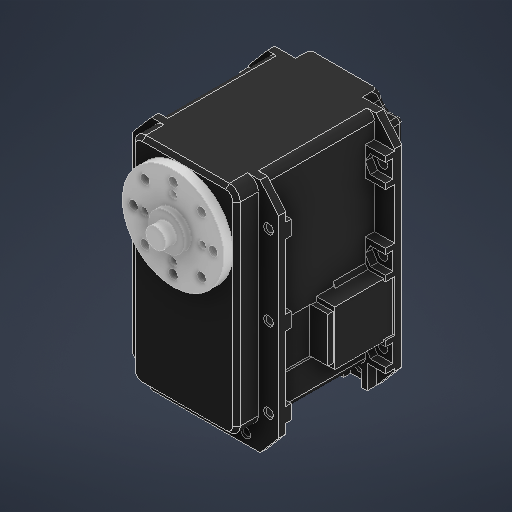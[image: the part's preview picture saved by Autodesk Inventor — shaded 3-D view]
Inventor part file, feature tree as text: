
AUTODESK INVENTOR PART (.ipt)
format: ipt  version: 2025 (Build 290162000, 162)  size: 522,752 bytes
history: native  units: in
note: dims shown in document units (in); Inventor stores cm internally (conversion verified against a paired STEP export)
features: thread x8, sketch x3, extrude x1, imported_body x1
ambient origin geometry x8: Origin, YZ Plane, XZ Plane, XY Plane, X Axis, Y Axis, Z Axis, Center Point
bodies: Solid1 (feature_tree)
feature tree (13):
  extrude  "Extrusion1"  Depth=0.315in
  thread  "Thread1"  [1 undecoded]
  thread  "Thread2"  [1 undecoded]
  thread  "Thread3"  [1 undecoded]
  thread  "Thread4"  [1 undecoded]
  thread  "Thread5"  [1 undecoded]
  thread  "Thread6"  [1 undecoded]
  thread  "Thread7"  [1 undecoded]
  thread  "Thread8"  [1 undecoded]
  sketch  "Sketch1"  dims[d0=0.0787in d1=0.315in d2=1.5748in d4=360.0deg d6=0.0984in d7=0.4331in d8=3.1496in d10=360.0deg d12=0.0in d13=0.0in d14=0.0984in d15=0.0in d16=0.0984in d17=0.0in d18=0.0984in d19=0.0in]
  sketch  "Sketch Circular Pattern1"  dims[d20=0.0984in d21=0.0in]
  sketch  "Sketch Circular Pattern2"  dims[d22=0.0984in d23=0.0in d24=0.0984in d25=0.0in d26=0.0984in d27=0.0in d28=0.0984in d29=0.0in]
  imported_body  "Base1"
note: 8 required parameter values undecoded (feature->parameter linkage not recoverable at this tier; creation-order binding heuristic only, values carry confidence <= 0.55)
